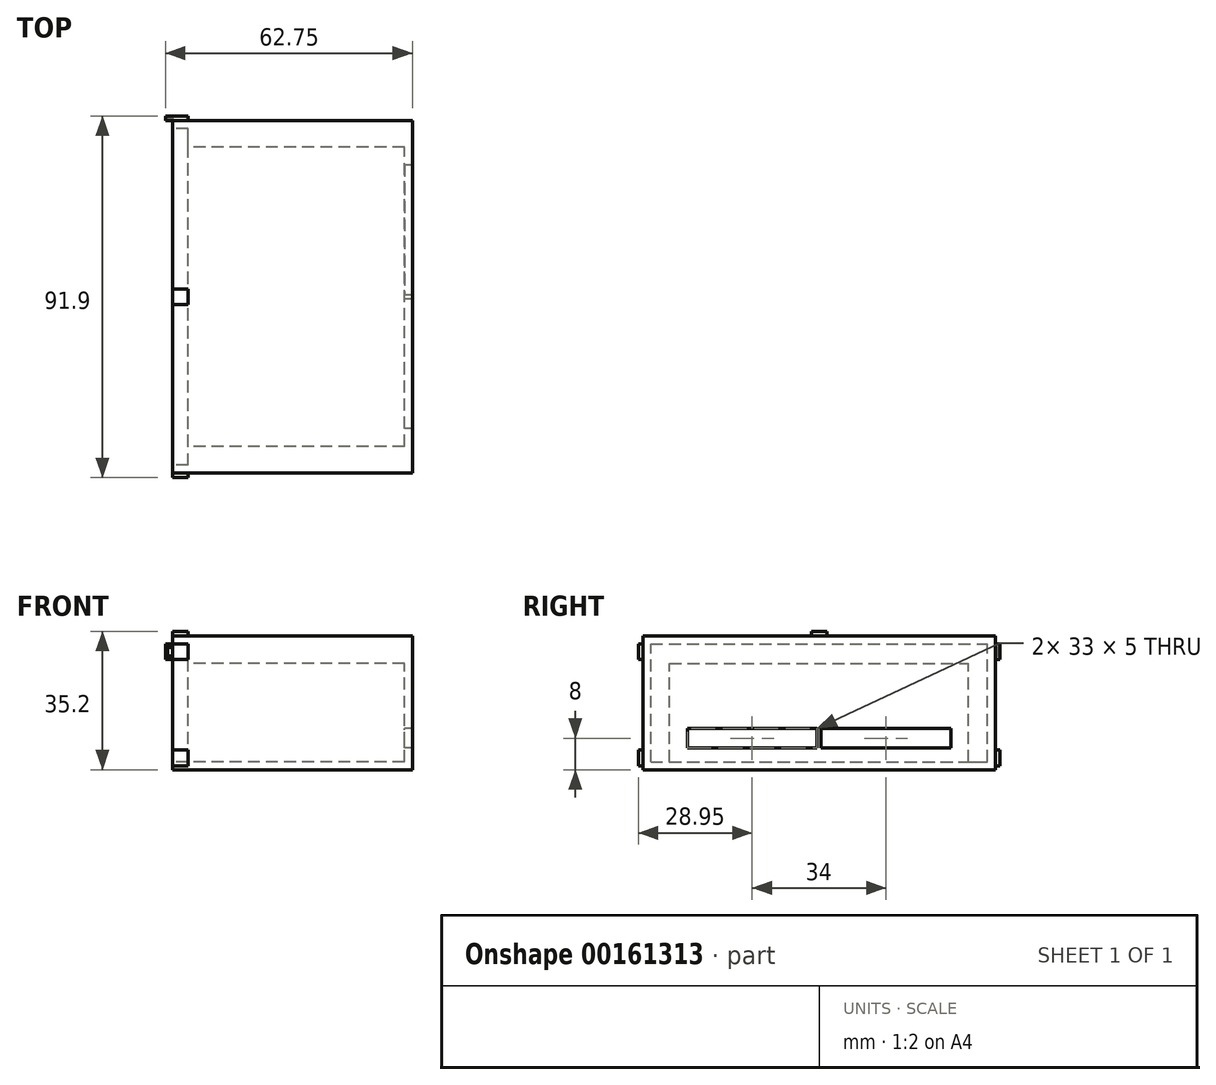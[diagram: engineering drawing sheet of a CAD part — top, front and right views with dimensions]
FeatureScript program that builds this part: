
annotation { "Feature Type Name" : "Feature", "Feature Type Description" : "" }
export const myFeature = defineFeature(function(context is Context, id is Id, definition is map)
    precondition{}
    {
        {
            var Q0;
            Q0=qCreatedBy(makeId("Right.planeOp"),FACE);
            var sketch = newSketch(context, id + "F0", { "sketchPlane" : qUnion([Q0])});
            skLineSegment(sketch, "E0.bottom", {"start": v(0, 0) * mm, "end": v(85.5, 0) * mm});
            skLineSegment(sketch, "E0.top", {"start": v(0, 30) * mm, "end": v(85.5, 30) * mm});
            skLineSegment(sketch, "E0.left", {"start": v(0, 0) * mm, "end": v(0, 30) * mm});
            skLineSegment(sketch, "E0.right", {"start": v(85.5, 0) * mm, "end": v(85.5, 30) * mm});
            skLineSegment(sketch, "E1.0", {"start": v(-2, 32) * mm, "end": v(87.5, 32) * mm});
            skLineSegment(sketch, "E1.1", {"start": v(-2, -2) * mm, "end": v(-2, 32) * mm});
            skLineSegment(sketch, "E1.2", {"start": v(-2, -2) * mm, "end": v(87.5, -2) * mm});
            skLineSegment(sketch, "E1.3", {"start": v(87.5, -2) * mm, "end": v(87.5, 32) * mm});
            skLineSegment(sketch, "E2", {"start": v(42.75, 32) * mm, "end": v(42.75, 40.72) * mm, "construction": true});
            skLineSegment(sketch, "E3", {"start": v(44.75, 33.2) * mm, "end": v(42.75, 33.2) * mm});
            skLineSegment(sketch, "E4", {"start": v(44.75, 33.2) * mm, "end": v(44.75, 32) * mm});
            skLineSegment(sketch, "E5.MirrorCS", {"start": v(40.75, 33.2) * mm, "end": v(42.75, 33.2) * mm});
            skLineSegment(sketch, "E6.MirrorCS", {"start": v(40.75, 33.2) * mm, "end": v(40.75, 32) * mm});
            skLineSegment(sketch, "E7.bottom", {"start": v(-2, 26) * mm, "end": v(-3.2, 26) * mm});
            skLineSegment(sketch, "E7.top", {"start": v(-2, 30) * mm, "end": v(-3.2, 30) * mm});
            skLineSegment(sketch, "E7.left", {"start": v(-2, 26) * mm, "end": v(-2, 30) * mm});
            skLineSegment(sketch, "E7.right", {"start": v(-3.2, 26) * mm, "end": v(-3.2, 30) * mm});
            skLineSegment(sketch, "E8.bottom", {"start": v(-2, -1) * mm, "end": v(-3.2, -1) * mm});
            skLineSegment(sketch, "E8.top", {"start": v(-2, 3) * mm, "end": v(-3.2, 3) * mm});
            skLineSegment(sketch, "E8.left", {"start": v(-2, -1) * mm, "end": v(-2, 3) * mm});
            skLineSegment(sketch, "E8.right", {"start": v(-3.2, -1) * mm, "end": v(-3.2, 3) * mm});
            skLineSegment(sketch, "E9.bottom", {"start": v(87.5, 26) * mm, "end": v(88.7, 26) * mm});
            skLineSegment(sketch, "E9.top", {"start": v(87.5, 30) * mm, "end": v(88.7, 30) * mm});
            skLineSegment(sketch, "E9.left", {"start": v(87.5, 26) * mm, "end": v(87.5, 30) * mm});
            skLineSegment(sketch, "E9.right", {"start": v(88.7, 26) * mm, "end": v(88.7, 30) * mm});
            skLineSegment(sketch, "E10.bottom", {"start": v(87.5, -1) * mm, "end": v(88.7, -1) * mm});
            skLineSegment(sketch, "E10.top", {"start": v(87.5, 3) * mm, "end": v(88.7, 3) * mm});
            skLineSegment(sketch, "E10.left", {"start": v(87.5, -1) * mm, "end": v(87.5, 3) * mm});
            skLineSegment(sketch, "E10.right", {"start": v(88.7, -1) * mm, "end": v(88.7, 3) * mm});
            skSolve(sketch);
        }
        {
            var Q0;
            Q0 = qSketchRegion(id + "F0", true);
            extrude(context, id + "F1", {"entities" : qUnion([Q0]), "depth" : 4 * mm});
        }
        {
            var Q0;
            Q0=makeQuery(id+"F1.opExtrude","CAP_FACE",FACE,{"disambiguationData":[OSD([sQuery(id+"F0.wireOp",EDGE,"E0.bottom"),sQuery(id+"F0.wireOp",EDGE,"E0.top"),sQuery(id+"F0.wireOp",EDGE,"E0.left"),sQuery(id+"F0.wireOp",EDGE,"E0.right"),sQuery(id+"F0.wireOp",EDGE,"E1.0"),sQuery(id+"F0.wireOp",EDGE,"E1.1"),sQuery(id+"F0.wireOp",EDGE,"E1.2"),sQuery(id+"F0.wireOp",EDGE,"E1.3"),sQuery(id+"F0.wireOp",EDGE,"E3"),sQuery(id+"F0.wireOp",EDGE,"E4"),sQuery(id+"F0.wireOp",EDGE,"E5.MirrorCS"),sQuery(id+"F0.wireOp",EDGE,"E6.MirrorCS"),sQuery(id+"F0.wireOp",EDGE,"E7.bottom"),sQuery(id+"F0.wireOp",EDGE,"E7.top"),sQuery(id+"F0.wireOp",EDGE,"E7.right"),sQuery(id+"F0.wireOp",EDGE,"E8.bottom"),sQuery(id+"F0.wireOp",EDGE,"E8.top"),sQuery(id+"F0.wireOp",EDGE,"E8.right"),sQuery(id+"F0.wireOp",EDGE,"E9.bottom"),sQuery(id+"F0.wireOp",EDGE,"E9.top"),sQuery(id+"F0.wireOp",EDGE,"E9.right"),sQuery(id+"F0.wireOp",EDGE,"E10.bottom"),sQuery(id+"F0.wireOp",EDGE,"E10.top"),sQuery(id+"F0.wireOp",EDGE,"E10.right")])],"isStart":false});
            var sketch = newSketch(context, id + "F2", { "sketchPlane" : qUnion([Q0])});
            skLineSegment(sketch, "E11.bottom", {"start": v(-2, 32) * mm, "end": v(87.5, 32) * mm});
            skLineSegment(sketch, "E11.top", {"start": v(-2, -2) * mm, "end": v(87.5, -2) * mm});
            skLineSegment(sketch, "E11.left", {"start": v(-2, 32) * mm, "end": v(-2, -2) * mm});
            skLineSegment(sketch, "E11.right", {"start": v(87.5, 32) * mm, "end": v(87.5, -2) * mm});
            skLineSegment(sketch, "E12", {"start": v(42.75, 32) * mm, "end": v(42.75, -2) * mm, "construction": true});
            skLineSegment(sketch, "E13", {"start": v(4.75, 0) * mm, "end": v(42.75, 0) * mm});
            skLineSegment(sketch, "E14", {"start": v(4.75, 0) * mm, "end": v(4.75, 25) * mm});
            skLineSegment(sketch, "E15", {"start": v(4.75, 25) * mm, "end": v(42.75, 25) * mm});
            skLineSegment(sketch, "E16.MirrorCS", {"start": v(80.75, 25) * mm, "end": v(42.75, 25) * mm});
            skLineSegment(sketch, "E17.MirrorCS", {"start": v(80.75, 0) * mm, "end": v(80.75, 25) * mm});
            skLineSegment(sketch, "E18.MirrorCS", {"start": v(80.75, 0) * mm, "end": v(42.75, 0) * mm});
            skSolve(sketch);
        }
        {
            var Q0;
            Q0 = qSketchRegion(id + "F2", true);
            extrude(context, id + "F3", {"entities" : qUnion([Q0]), "operationType" : NewBodyOperationType.ADD, "depth" : 55 * mm});
        }
        {
            var Q0;
            Q0=makeQuery(id+"F3.opExtrude","CAP_FACE",FACE,{"disambiguationData":[OSD([sQuery(id+"F2.wireOp",EDGE,"E11.bottom"),sQuery(id+"F2.wireOp",EDGE,"E11.top"),sQuery(id+"F2.wireOp",EDGE,"E11.left"),sQuery(id+"F2.wireOp",EDGE,"E11.right"),sQuery(id+"F2.wireOp",EDGE,"E13"),sQuery(id+"F2.wireOp",EDGE,"E14"),sQuery(id+"F2.wireOp",EDGE,"E15"),sQuery(id+"F2.wireOp",EDGE,"E16.MirrorCS"),sQuery(id+"F2.wireOp",EDGE,"E17.MirrorCS"),sQuery(id+"F2.wireOp",EDGE,"E18.MirrorCS")])],"isStart":false});
            var sketch = newSketch(context, id + "F4", { "sketchPlane" : qUnion([Q0])});
            skLineSegment(sketch, "E19.bottom", {"start": v(-2, 32) * mm, "end": v(87.5, 32) * mm});
            skLineSegment(sketch, "E19.top", {"start": v(-2, -2) * mm, "end": v(87.5, -2) * mm});
            skLineSegment(sketch, "E19.left", {"start": v(-2, 32) * mm, "end": v(-2, -2) * mm});
            skLineSegment(sketch, "E19.right", {"start": v(87.5, 32) * mm, "end": v(87.5, -2) * mm});
            skLineSegment(sketch, "E20.bottom", {"start": v(9.25, 3.5) * mm, "end": v(42.25, 3.5) * mm});
            skLineSegment(sketch, "E20.top", {"start": v(9.25, 8.5) * mm, "end": v(42.25, 8.5) * mm});
            skLineSegment(sketch, "E20.left", {"start": v(9.25, 3.5) * mm, "end": v(9.25, 8.5) * mm});
            skLineSegment(sketch, "E20.right", {"start": v(42.25, 3.5) * mm, "end": v(42.25, 8.5) * mm});
            skLineSegment(sketch, "E21", {"start": v(42.75, 32) * mm, "end": v(42.75, -2) * mm, "construction": true});
            skLineSegment(sketch, "E22.MirrorCS", {"start": v(76.25, 8.5) * mm, "end": v(43.25, 8.5) * mm});
            skLineSegment(sketch, "E23.MirrorCS", {"start": v(76.25, 3.5) * mm, "end": v(76.25, 8.5) * mm});
            skLineSegment(sketch, "E24.MirrorCS", {"start": v(76.25, 3.5) * mm, "end": v(43.25, 3.5) * mm});
            skLineSegment(sketch, "E25.MirrorCS", {"start": v(43.25, 3.5) * mm, "end": v(43.25, 8.5) * mm});
            skSolve(sketch);
        }
        {
            var Q0;
            Q0 = qSketchRegion(id + "F4", true);
            extrude(context, id + "F5", {"entities" : qUnion([Q0]), "operationType" : NewBodyOperationType.ADD, "depth" : 2 * mm});
        }
        {
            var Q0;
            Q0=makeQuery(id+"F1.opExtrude","CAP_FACE",FACE,{"disambiguationData":[OSD([sQuery(id+"F0.wireOp",EDGE,"E0.bottom"),sQuery(id+"F0.wireOp",EDGE,"E0.top"),sQuery(id+"F0.wireOp",EDGE,"E0.left"),sQuery(id+"F0.wireOp",EDGE,"E0.right"),sQuery(id+"F0.wireOp",EDGE,"E1.0"),sQuery(id+"F0.wireOp",EDGE,"E1.1"),sQuery(id+"F0.wireOp",EDGE,"E1.2"),sQuery(id+"F0.wireOp",EDGE,"E1.3"),sQuery(id+"F0.wireOp",EDGE,"E3"),sQuery(id+"F0.wireOp",EDGE,"E4"),sQuery(id+"F0.wireOp",EDGE,"E5.MirrorCS"),sQuery(id+"F0.wireOp",EDGE,"E6.MirrorCS"),sQuery(id+"F0.wireOp",EDGE,"E7.bottom"),sQuery(id+"F0.wireOp",EDGE,"E7.top"),sQuery(id+"F0.wireOp",EDGE,"E7.right"),sQuery(id+"F0.wireOp",EDGE,"E8.bottom"),sQuery(id+"F0.wireOp",EDGE,"E8.top"),sQuery(id+"F0.wireOp",EDGE,"E8.right"),sQuery(id+"F0.wireOp",EDGE,"E9.bottom"),sQuery(id+"F0.wireOp",EDGE,"E9.top"),sQuery(id+"F0.wireOp",EDGE,"E9.right"),sQuery(id+"F0.wireOp",EDGE,"E10.bottom"),sQuery(id+"F0.wireOp",EDGE,"E10.top"),sQuery(id+"F0.wireOp",EDGE,"E10.right")])],"isStart":true});
            var sketch = newSketch(context, id + "F6", { "sketchPlane" : qUnion([Q0])});
            skLineSegment(sketch, "E26", {"start": v(-87.5, 30) * mm, "end": v(-88.7, 30) * mm});
            skLineSegment(sketch, "E27", {"start": v(-88.7, 30) * mm, "end": v(-88.7, 26) * mm});
            skLineSegment(sketch, "E28", {"start": v(-88.7, 26) * mm, "end": v(-87.5, 26) * mm});
            skLineSegment(sketch, "E29", {"start": v(-87.5, 26) * mm, "end": v(-87.5, 26.9) * mm});
            skLineSegment(sketch, "E30", {"start": v(-87.5, 26.9) * mm, "end": v(-88.15, 26.9) * mm});
            skLineSegment(sketch, "E31", {"start": v(-88.15, 26.9) * mm, "end": v(-88.15, 29.1) * mm});
            skLineSegment(sketch, "E32", {"start": v(-88.15, 29.1) * mm, "end": v(-87.5, 29.1) * mm});
            skLineSegment(sketch, "E33", {"start": v(-87.5, 29.1) * mm, "end": v(-87.5, 30) * mm});
            skSolve(sketch);
        }
        {
            var Q0;
            Q0=makeQuery(id+"F6.imprint","IMPRINT",FACE,{"disambiguationData":[TD([[makeQuery(id+"F6.imprint","IMPRINT",EDGE,{"derivedFrom":sQuery(id+"F6.wireOp",EDGE,"E26")}),1.0]])]});
            extrude(context, id + "F7", {"entities" : qUnion([Q0]), "operationType" : NewBodyOperationType.ADD, "depth" : 1.25 * mm});
        }
        {
            var Q0;
            Q0=makeQuery(id+"F7.opExtrude","CAP_FACE",FACE,{"disambiguationData":[OSD([sQuery(id+"F6.wireOp",EDGE,"E26"),sQuery(id+"F6.wireOp",EDGE,"E27"),sQuery(id+"F6.wireOp",EDGE,"E28"),sQuery(id+"F6.wireOp",EDGE,"E29"),sQuery(id+"F6.wireOp",EDGE,"E30"),sQuery(id+"F6.wireOp",EDGE,"E31"),sQuery(id+"F6.wireOp",EDGE,"E32"),sQuery(id+"F6.wireOp",EDGE,"E33")])],"isStart":false});
            var sketch = newSketch(context, id + "F8", { "sketchPlane" : qUnion([Q0])});
            skLineSegment(sketch, "E34.bottom", {"start": v(-88.7, 30) * mm, "end": v(-87.5, 30) * mm});
            skLineSegment(sketch, "E34.top", {"start": v(-88.7, 26) * mm, "end": v(-87.5, 26) * mm});
            skLineSegment(sketch, "E34.left", {"start": v(-88.7, 30) * mm, "end": v(-88.7, 26) * mm});
            skLineSegment(sketch, "E34.right", {"start": v(-87.5, 30) * mm, "end": v(-87.5, 26) * mm});
            skSolve(sketch);
        }
        {
            var Q0;
            Q0 = qSketchRegion(id + "F8", true);
            extrude(context, id + "F9", {"entities" : qUnion([Q0]), "operationType" : NewBodyOperationType.ADD, "depth" : .5 * mm});
        }
    });
